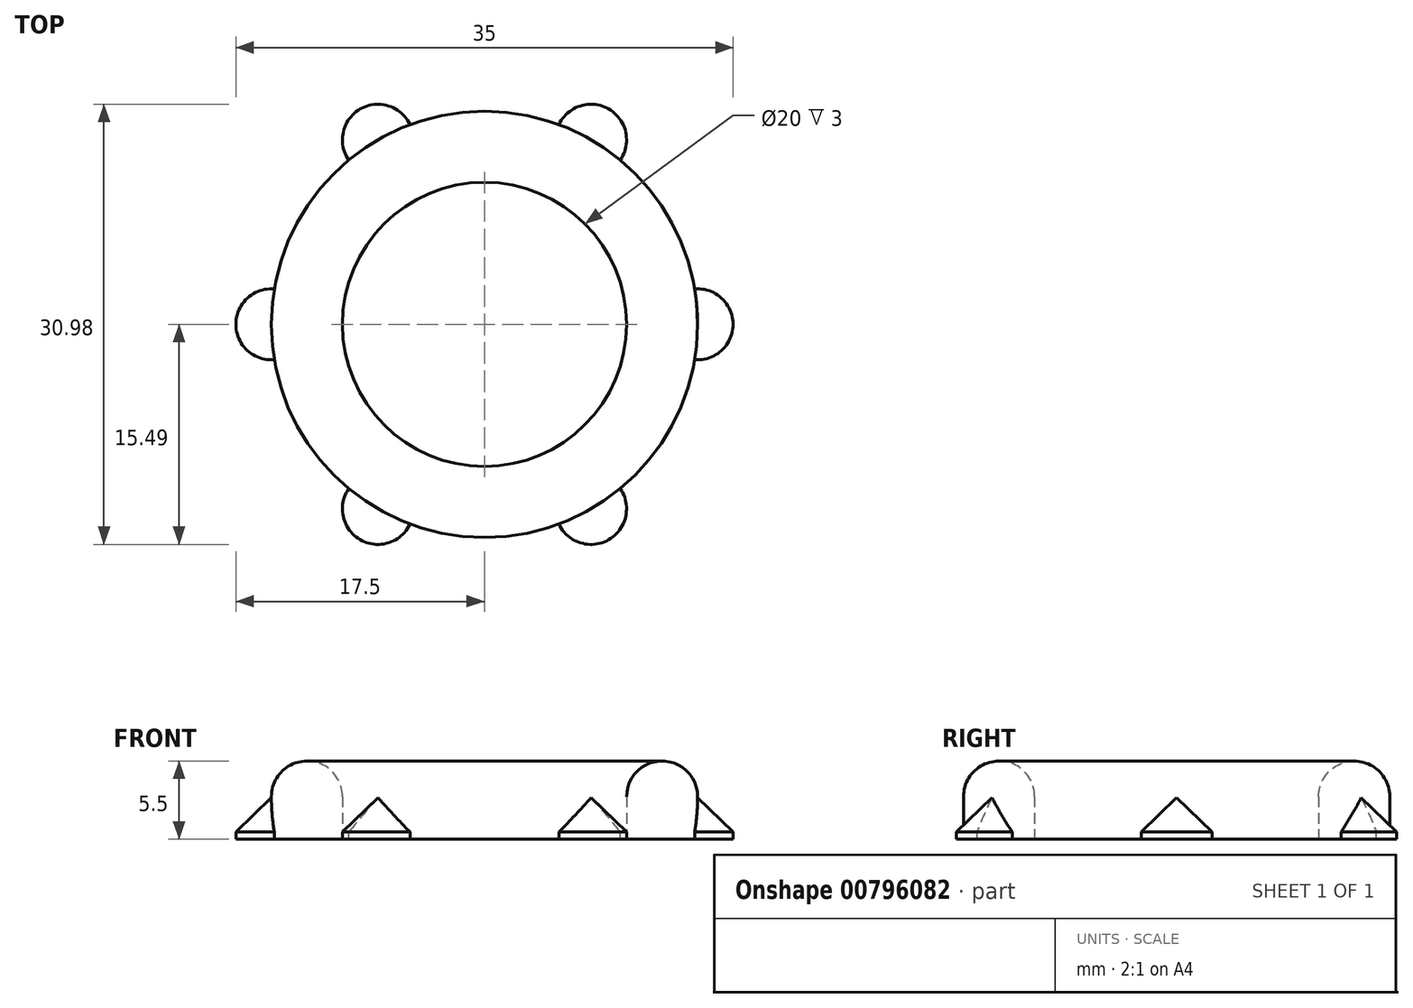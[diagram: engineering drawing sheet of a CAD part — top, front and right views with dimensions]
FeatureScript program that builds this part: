
annotation { "Feature Type Name" : "Feature", "Feature Type Description" : "" }
export const myFeature = defineFeature(function(context is Context, id is Id, definition is map)
    precondition{}
    {
        {
            var Q0;
            Q0=qCreatedBy(makeId("Top.planeOp"),FACE);
            var sketch = newSketch(context, id + "F0", { "sketchPlane" : qUnion([Q0])});
            skCircle(sketch, "E0", {"center": v(0, 0) * mm, "radius": 15 * mm});
            skCircle(sketch, "E1", {"center": v(0, 0) * mm, "radius": 10 * mm});
            skCircle(sketch, "E2", {"center": v(0, 0) * mm, "radius": 12.5 * mm, "construction": true});
            skSolve(sketch);
        }
        {
            var Q0;
            Q0=qCreatedBy(makeId("Top.planeOp"),FACE);
            var sketch = newSketch(context, id + "F1", { "sketchPlane" : qUnion([Q0])});
            skCircle(sketch, "E3.0", {"center": v(0, 0) * mm, "radius": 15 * mm});
            skCircle(sketch, "E4", {"center": v(-15, 0) * mm, "radius": 2.5 * mm});
            skCircle(sketch, "E5.1.0", {"center": v(-7.5, -13) * mm, "radius": 2.5 * mm});
            skCircle(sketch, "E5.2.0", {"center": v(7.5, -13) * mm, "radius": 2.5 * mm});
            skCircle(sketch, "E5.3.0", {"center": v(15, 0) * mm, "radius": 2.5 * mm});
            skCircle(sketch, "E5.4.0", {"center": v(7.5, 13) * mm, "radius": 2.5 * mm});
            skCircle(sketch, "E5.5.0", {"center": v(-7.5, 13) * mm, "radius": 2.5 * mm});
            skSolve(sketch);
        }
        {
            var Q0;
            {var subQ0=sQuery(id+"F0.wireOp",EDGE,"a43ba777-b534-4697-9f40-372b6a1b8b84.2.0");var subQ1=sQuery(id+"F0.wireOp",EDGE,"E0");var subQ2=makeQuery(id+"F0.imprint","INTERSECT",VERTEX,{"disambiguationData":[OD(0.0)],"derivedFrom":[subQ1,subQ0]});Q0=makeQuery(id+"F0.imprint","IMPRINT",FACE,{"disambiguationData":[TD([[makeQuery(id+"F0.imprint","IMPRINT",EDGE,{"disambiguationData":[TD([[subQ2,1.0]])],"derivedFrom":subQ1}),1.0]])]});}
            var Q1;
            {var subQ0=sQuery(id+"F0.wireOp",EDGE,"a43ba777-b534-4697-9f40-372b6a1b8b84.3.0");var subQ1=sQuery(id+"F0.wireOp",EDGE,"E0");var subQ2=makeQuery(id+"F0.imprint","INTERSECT",VERTEX,{"disambiguationData":[OD(0.0)],"derivedFrom":[subQ1,subQ0]});Q1=makeQuery(id+"F0.imprint","IMPRINT",FACE,{"disambiguationData":[TD([[makeQuery(id+"F0.imprint","IMPRINT",EDGE,{"disambiguationData":[TD([[subQ2,-1.0]])],"derivedFrom":subQ1}),1.0]])]});}
            var Q2;
            {var subQ0=sQuery(id+"F0.wireOp",EDGE,"a43ba777-b534-4697-9f40-372b6a1b8b84.4.0");var subQ1=sQuery(id+"F0.wireOp",EDGE,"E0");var subQ2=makeQuery(id+"F0.imprint","INTERSECT",VERTEX,{"disambiguationData":[OD(0.0)],"derivedFrom":[subQ1,subQ0]});Q2=makeQuery(id+"F0.imprint","IMPRINT",FACE,{"disambiguationData":[TD([[makeQuery(id+"F0.imprint","IMPRINT",EDGE,{"disambiguationData":[TD([[subQ2,-1.0]])],"derivedFrom":subQ1}),1.0]])]});}
            var Q3;
            {var subQ0=sQuery(id+"F0.wireOp",EDGE,"a43ba777-b534-4697-9f40-372b6a1b8b84.5.0");var subQ1=sQuery(id+"F0.wireOp",EDGE,"E0");var subQ2=makeQuery(id+"F0.imprint","INTERSECT",VERTEX,{"disambiguationData":[OD(0.0)],"derivedFrom":[subQ1,subQ0]});Q3=makeQuery(id+"F0.imprint","IMPRINT",FACE,{"disambiguationData":[TD([[makeQuery(id+"F0.imprint","IMPRINT",EDGE,{"disambiguationData":[TD([[subQ2,-1.0]])],"derivedFrom":subQ1}),1.0]])]});}
            var Q4;
            {var subQ0=sQuery(id+"F0.wireOp",EDGE,"MEjsecI2-ZT2x-rk5m-w1Sc-rnXZrPzxG7gC");var subQ1=sQuery(id+"F0.wireOp",EDGE,"E0");var subQ2=makeQuery(id+"F0.imprint","INTERSECT",VERTEX,{"disambiguationData":[OD(0.0)],"derivedFrom":[subQ1,subQ0]});Q4=makeQuery(id+"F0.imprint","IMPRINT",FACE,{"disambiguationData":[TD([[makeQuery(id+"F0.imprint","IMPRINT",EDGE,{"disambiguationData":[TD([[subQ2,-1.0]])],"derivedFrom":subQ1}),1.0]])]});}
            var Q5;
            {var subQ0=sQuery(id+"F0.wireOp",EDGE,"a43ba777-b534-4697-9f40-372b6a1b8b84.1.0");var subQ1=sQuery(id+"F0.wireOp",EDGE,"E0");var subQ2=makeQuery(id+"F0.imprint","INTERSECT",VERTEX,{"disambiguationData":[OD(0.0)],"derivedFrom":[subQ1,subQ0]});Q5=makeQuery(id+"F0.imprint","IMPRINT",FACE,{"disambiguationData":[TD([[makeQuery(id+"F0.imprint","IMPRINT",EDGE,{"disambiguationData":[TD([[subQ2,-1.0]])],"derivedFrom":subQ1}),1.0]])]});}
            var Q6;
            Q6=makeQuery(id+"F0.imprint","IMPRINT",FACE,{"disambiguationData":[TD([[makeQuery(id+"F0.imprint","IMPRINT",EDGE,{"derivedFrom":sQuery(id+"F0.wireOp",EDGE,"E1")}),-1.0]])]});
            extrude(context, id + "F2", {"entities" : qUnion([Q0, Q1, Q2, Q3, Q4, Q5, Q6]), "depth" : 5 * mm, "offsetDistance" : 25 * mm});
        }
        {
            var Q0;
            Q0=makeQuery(id+"F2.opExtrude","CAP_FACE",FACE,{"disambiguationData":[OSD([sQuery(id+"F0.wireOp",EDGE,"E0"),sQuery(id+"F0.wireOp",EDGE,"E1")])],"isStart":false});
            fillet(context, id + "F3", {"entities" : qUnion([Q0]), "radius" : 2.5 * mm, "tangentPropagation" : true, "allowEdgeOverflow" : false});
        }
        {
            var Q0;
            {var subQ0=sQuery(id+"F1.wireOp",EDGE,"E5.1.0");var subQ1=sQuery(id+"F1.wireOp",EDGE,"E3.0");var subQ2=makeQuery(id+"F1.imprint","INTERSECT",VERTEX,{"disambiguationData":[OD(0.0)],"derivedFrom":[subQ1,subQ0]});Q0=makeQuery(id+"F1.imprint","IMPRINT",FACE,{"disambiguationData":[TD([[makeQuery(id+"F1.imprint","IMPRINT",EDGE,{"disambiguationData":[TD([[subQ2,-1.0]])],"derivedFrom":subQ1}),1.0]])]});}
            var Q1;
            {var subQ0=sQuery(id+"F1.wireOp",EDGE,"E4");var subQ1=sQuery(id+"F1.wireOp",EDGE,"E3.0");var subQ2=makeQuery(id+"F1.imprint","INTERSECT",VERTEX,{"disambiguationData":[OD(0.0)],"derivedFrom":[subQ1,subQ0]});Q1=makeQuery(id+"F1.imprint","IMPRINT",FACE,{"disambiguationData":[TD([[makeQuery(id+"F1.imprint","IMPRINT",EDGE,{"disambiguationData":[TD([[subQ2,-1.0]])],"derivedFrom":subQ1}),1.0]])]});}
            var Q2;
            {var subQ0=sQuery(id+"F1.wireOp",EDGE,"E5.5.0");var subQ1=sQuery(id+"F1.wireOp",EDGE,"E3.0");var subQ2=makeQuery(id+"F1.imprint","INTERSECT",VERTEX,{"disambiguationData":[OD(0.0)],"derivedFrom":[subQ1,subQ0]});Q2=makeQuery(id+"F1.imprint","IMPRINT",FACE,{"disambiguationData":[TD([[makeQuery(id+"F1.imprint","IMPRINT",EDGE,{"disambiguationData":[TD([[subQ2,-1.0]])],"derivedFrom":subQ1}),1.0]])]});}
            var Q3;
            {var subQ0=sQuery(id+"F1.wireOp",EDGE,"E5.4.0");var subQ1=sQuery(id+"F1.wireOp",EDGE,"E3.0");var subQ2=makeQuery(id+"F1.imprint","INTERSECT",VERTEX,{"disambiguationData":[OD(0.0)],"derivedFrom":[subQ1,subQ0]});Q3=makeQuery(id+"F1.imprint","IMPRINT",FACE,{"disambiguationData":[TD([[makeQuery(id+"F1.imprint","IMPRINT",EDGE,{"disambiguationData":[TD([[subQ2,-1.0]])],"derivedFrom":subQ1}),1.0]])]});}
            var Q4;
            {var subQ0=sQuery(id+"F1.wireOp",EDGE,"E5.3.0");var subQ1=sQuery(id+"F1.wireOp",EDGE,"E3.0");var subQ2=makeQuery(id+"F1.imprint","INTERSECT",VERTEX,{"disambiguationData":[OD(0.0)],"derivedFrom":[subQ1,subQ0]});Q4=makeQuery(id+"F1.imprint","IMPRINT",FACE,{"disambiguationData":[TD([[makeQuery(id+"F1.imprint","IMPRINT",EDGE,{"disambiguationData":[TD([[subQ2,1.0]])],"derivedFrom":subQ1}),1.0]])]});}
            var Q5;
            {var subQ0=sQuery(id+"F1.wireOp",EDGE,"E5.2.0");var subQ1=sQuery(id+"F1.wireOp",EDGE,"E3.0");var subQ2=makeQuery(id+"F1.imprint","INTERSECT",VERTEX,{"disambiguationData":[OD(0.0)],"derivedFrom":[subQ1,subQ0]});Q5=makeQuery(id+"F1.imprint","IMPRINT",FACE,{"disambiguationData":[TD([[makeQuery(id+"F1.imprint","IMPRINT",EDGE,{"disambiguationData":[TD([[subQ2,-1.0]])],"derivedFrom":subQ1}),1.0]])]});}
            var Q6;
            {var subQ0=sQuery(id+"F1.wireOp",EDGE,"E5.2.0");var subQ1=sQuery(id+"F1.wireOp",EDGE,"E3.0");var subQ2=makeQuery(id+"F1.imprint","INTERSECT",VERTEX,{"disambiguationData":[OD(0.0)],"derivedFrom":[subQ1,subQ0]});Q6=makeQuery(id+"F1.imprint","IMPRINT",FACE,{"disambiguationData":[TD([[makeQuery(id+"F1.imprint","IMPRINT",EDGE,{"disambiguationData":[TD([[subQ2,-1.0]])],"derivedFrom":subQ1}),-1.0]])]});}
            var Q7;
            {var subQ0=sQuery(id+"F1.wireOp",EDGE,"E5.3.0");var subQ1=sQuery(id+"F1.wireOp",EDGE,"E3.0");var subQ2=makeQuery(id+"F1.imprint","INTERSECT",VERTEX,{"disambiguationData":[OD(0.0)],"derivedFrom":[subQ1,subQ0]});Q7=makeQuery(id+"F1.imprint","IMPRINT",FACE,{"disambiguationData":[TD([[makeQuery(id+"F1.imprint","IMPRINT",EDGE,{"disambiguationData":[TD([[subQ2,1.0]])],"derivedFrom":subQ1}),-1.0]])]});}
            var Q8;
            {var subQ0=sQuery(id+"F1.wireOp",EDGE,"E5.4.0");var subQ1=sQuery(id+"F1.wireOp",EDGE,"E3.0");var subQ2=makeQuery(id+"F1.imprint","INTERSECT",VERTEX,{"disambiguationData":[OD(0.0)],"derivedFrom":[subQ1,subQ0]});Q8=makeQuery(id+"F1.imprint","IMPRINT",FACE,{"disambiguationData":[TD([[makeQuery(id+"F1.imprint","IMPRINT",EDGE,{"disambiguationData":[TD([[subQ2,-1.0]])],"derivedFrom":subQ1}),-1.0]])]});}
            var Q9;
            {var subQ0=sQuery(id+"F1.wireOp",EDGE,"E5.5.0");var subQ1=sQuery(id+"F1.wireOp",EDGE,"E3.0");var subQ2=makeQuery(id+"F1.imprint","INTERSECT",VERTEX,{"disambiguationData":[OD(0.0)],"derivedFrom":[subQ1,subQ0]});Q9=makeQuery(id+"F1.imprint","IMPRINT",FACE,{"disambiguationData":[TD([[makeQuery(id+"F1.imprint","IMPRINT",EDGE,{"disambiguationData":[TD([[subQ2,-1.0]])],"derivedFrom":subQ1}),-1.0]])]});}
            var Q10;
            {var subQ0=sQuery(id+"F1.wireOp",EDGE,"E4");var subQ1=sQuery(id+"F1.wireOp",EDGE,"E3.0");var subQ2=makeQuery(id+"F1.imprint","INTERSECT",VERTEX,{"disambiguationData":[OD(0.0)],"derivedFrom":[subQ1,subQ0]});Q10=makeQuery(id+"F1.imprint","IMPRINT",FACE,{"disambiguationData":[TD([[makeQuery(id+"F1.imprint","IMPRINT",EDGE,{"disambiguationData":[TD([[subQ2,-1.0]])],"derivedFrom":subQ1}),-1.0]])]});}
            var Q11;
            {var subQ0=sQuery(id+"F1.wireOp",EDGE,"E5.1.0");var subQ1=sQuery(id+"F1.wireOp",EDGE,"E3.0");var subQ2=makeQuery(id+"F1.imprint","INTERSECT",VERTEX,{"disambiguationData":[OD(0.0)],"derivedFrom":[subQ1,subQ0]});Q11=makeQuery(id+"F1.imprint","IMPRINT",FACE,{"disambiguationData":[TD([[makeQuery(id+"F1.imprint","IMPRINT",EDGE,{"disambiguationData":[TD([[subQ2,-1.0]])],"derivedFrom":subQ1}),-1.0]])]});}
            extrude(context, id + "F4", {"entities" : qUnion([Q0, Q1, Q2, Q3, Q4, Q5, Q6, Q7, Q8, Q9, Q10, Q11]), "operationType" : NewBodyOperationType.ADD, "depth" : 3 * mm, "offsetDistance" : 25 * mm, "hasDraft" : true, "draftAngle" : 46 * degree, "draftPullDirection" : true});
        }
        {
            var Q0;
            {var subQ0=sQuery(id+"F1.wireOp",EDGE,"E4");var subQ1=sQuery(id+"F1.wireOp",EDGE,"E3.0");var subQ2=makeQuery(id+"F1.imprint","INTERSECT",VERTEX,{"disambiguationData":[OD(0.0)],"derivedFrom":[subQ1,subQ0]});Q0=makeQuery(id+"F1.imprint","IMPRINT",FACE,{"disambiguationData":[TD([[makeQuery(id+"F1.imprint","IMPRINT",EDGE,{"disambiguationData":[TD([[subQ2,-1.0]])],"derivedFrom":subQ1}),1.0]])]});}
            var Q1;
            {var subQ0=sQuery(id+"F1.wireOp",EDGE,"E4");var subQ1=sQuery(id+"F1.wireOp",EDGE,"E3.0");var subQ2=makeQuery(id+"F1.imprint","INTERSECT",VERTEX,{"disambiguationData":[OD(0.0)],"derivedFrom":[subQ1,subQ0]});Q1=makeQuery(id+"F1.imprint","IMPRINT",FACE,{"disambiguationData":[TD([[makeQuery(id+"F1.imprint","IMPRINT",EDGE,{"disambiguationData":[TD([[subQ2,-1.0]])],"derivedFrom":subQ1}),-1.0]])]});}
            var Q2;
            {var subQ0=sQuery(id+"F1.wireOp",EDGE,"E5.1.0");var subQ1=sQuery(id+"F1.wireOp",EDGE,"E3.0");var subQ2=makeQuery(id+"F1.imprint","INTERSECT",VERTEX,{"disambiguationData":[OD(0.0)],"derivedFrom":[subQ1,subQ0]});Q2=makeQuery(id+"F1.imprint","IMPRINT",FACE,{"disambiguationData":[TD([[makeQuery(id+"F1.imprint","IMPRINT",EDGE,{"disambiguationData":[TD([[subQ2,-1.0]])],"derivedFrom":subQ1}),-1.0]])]});}
            var Q3;
            {var subQ0=sQuery(id+"F1.wireOp",EDGE,"E5.1.0");var subQ1=sQuery(id+"F1.wireOp",EDGE,"E3.0");var subQ2=makeQuery(id+"F1.imprint","INTERSECT",VERTEX,{"disambiguationData":[OD(0.0)],"derivedFrom":[subQ1,subQ0]});Q3=makeQuery(id+"F1.imprint","IMPRINT",FACE,{"disambiguationData":[TD([[makeQuery(id+"F1.imprint","IMPRINT",EDGE,{"disambiguationData":[TD([[subQ2,-1.0]])],"derivedFrom":subQ1}),1.0]])]});}
            var Q4;
            {var subQ0=sQuery(id+"F1.wireOp",EDGE,"E5.2.0");var subQ1=sQuery(id+"F1.wireOp",EDGE,"E3.0");var subQ2=makeQuery(id+"F1.imprint","INTERSECT",VERTEX,{"disambiguationData":[OD(0.0)],"derivedFrom":[subQ1,subQ0]});Q4=makeQuery(id+"F1.imprint","IMPRINT",FACE,{"disambiguationData":[TD([[makeQuery(id+"F1.imprint","IMPRINT",EDGE,{"disambiguationData":[TD([[subQ2,-1.0]])],"derivedFrom":subQ1}),1.0]])]});}
            var Q5;
            {var subQ0=sQuery(id+"F1.wireOp",EDGE,"E5.2.0");var subQ1=sQuery(id+"F1.wireOp",EDGE,"E3.0");var subQ2=makeQuery(id+"F1.imprint","INTERSECT",VERTEX,{"disambiguationData":[OD(0.0)],"derivedFrom":[subQ1,subQ0]});Q5=makeQuery(id+"F1.imprint","IMPRINT",FACE,{"disambiguationData":[TD([[makeQuery(id+"F1.imprint","IMPRINT",EDGE,{"disambiguationData":[TD([[subQ2,-1.0]])],"derivedFrom":subQ1}),-1.0]])]});}
            var Q6;
            {var subQ0=sQuery(id+"F1.wireOp",EDGE,"E5.3.0");var subQ1=sQuery(id+"F1.wireOp",EDGE,"E3.0");var subQ2=makeQuery(id+"F1.imprint","INTERSECT",VERTEX,{"disambiguationData":[OD(0.0)],"derivedFrom":[subQ1,subQ0]});Q6=makeQuery(id+"F1.imprint","IMPRINT",FACE,{"disambiguationData":[TD([[makeQuery(id+"F1.imprint","IMPRINT",EDGE,{"disambiguationData":[TD([[subQ2,1.0]])],"derivedFrom":subQ1}),1.0]])]});}
            var Q7;
            {var subQ0=sQuery(id+"F1.wireOp",EDGE,"E5.3.0");var subQ1=sQuery(id+"F1.wireOp",EDGE,"E3.0");var subQ2=makeQuery(id+"F1.imprint","INTERSECT",VERTEX,{"disambiguationData":[OD(0.0)],"derivedFrom":[subQ1,subQ0]});Q7=makeQuery(id+"F1.imprint","IMPRINT",FACE,{"disambiguationData":[TD([[makeQuery(id+"F1.imprint","IMPRINT",EDGE,{"disambiguationData":[TD([[subQ2,1.0]])],"derivedFrom":subQ1}),-1.0]])]});}
            var Q8;
            {var subQ0=sQuery(id+"F1.wireOp",EDGE,"E5.4.0");var subQ1=sQuery(id+"F1.wireOp",EDGE,"E3.0");var subQ2=makeQuery(id+"F1.imprint","INTERSECT",VERTEX,{"disambiguationData":[OD(0.0)],"derivedFrom":[subQ1,subQ0]});Q8=makeQuery(id+"F1.imprint","IMPRINT",FACE,{"disambiguationData":[TD([[makeQuery(id+"F1.imprint","IMPRINT",EDGE,{"disambiguationData":[TD([[subQ2,-1.0]])],"derivedFrom":subQ1}),-1.0]])]});}
            var Q9;
            {var subQ0=sQuery(id+"F1.wireOp",EDGE,"E5.5.0");var subQ1=sQuery(id+"F1.wireOp",EDGE,"E3.0");var subQ2=makeQuery(id+"F1.imprint","INTERSECT",VERTEX,{"disambiguationData":[OD(0.0)],"derivedFrom":[subQ1,subQ0]});Q9=makeQuery(id+"F1.imprint","IMPRINT",FACE,{"disambiguationData":[TD([[makeQuery(id+"F1.imprint","IMPRINT",EDGE,{"disambiguationData":[TD([[subQ2,-1.0]])],"derivedFrom":subQ1}),-1.0]])]});}
            var Q10;
            {var subQ0=sQuery(id+"F1.wireOp",EDGE,"E5.5.0");var subQ1=sQuery(id+"F1.wireOp",EDGE,"E3.0");var subQ2=makeQuery(id+"F1.imprint","INTERSECT",VERTEX,{"disambiguationData":[OD(0.0)],"derivedFrom":[subQ1,subQ0]});Q10=makeQuery(id+"F1.imprint","IMPRINT",FACE,{"disambiguationData":[TD([[makeQuery(id+"F1.imprint","IMPRINT",EDGE,{"disambiguationData":[TD([[subQ2,-1.0]])],"derivedFrom":subQ1}),1.0]])]});}
            var Q11;
            {var subQ0=sQuery(id+"F1.wireOp",EDGE,"E5.4.0");var subQ1=sQuery(id+"F1.wireOp",EDGE,"E3.0");var subQ2=makeQuery(id+"F1.imprint","INTERSECT",VERTEX,{"disambiguationData":[OD(0.0)],"derivedFrom":[subQ1,subQ0]});Q11=makeQuery(id+"F1.imprint","IMPRINT",FACE,{"disambiguationData":[TD([[makeQuery(id+"F1.imprint","IMPRINT",EDGE,{"disambiguationData":[TD([[subQ2,-1.0]])],"derivedFrom":subQ1}),1.0]])]});}
            var Q12;
            Q12=makeQuery(id+"F0.imprint","IMPRINT",FACE,{"disambiguationData":[TD([[makeQuery(id+"F0.imprint","IMPRINT",EDGE,{"derivedFrom":sQuery(id+"F0.wireOp",EDGE,"E0")}),1.0]])]});
            extrude(context, id + "F5", {"entities" : qUnion([Q0, Q1, Q2, Q3, Q4, Q5, Q6, Q7, Q8, Q9, Q10, Q11, Q12]), "operationType" : NewBodyOperationType.ADD, "oppositeDirection" : true, "depth" : 0.5 * mm, "offsetDistance" : 25 * mm});
        }
    });
